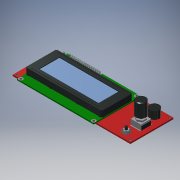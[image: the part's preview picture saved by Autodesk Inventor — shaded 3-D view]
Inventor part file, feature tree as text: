
AUTODESK INVENTOR PART (.ipt)
format: ipt  version: 2018 (Build 220112000, 112)  size: 651,776 bytes
history: native  units: mm
features: chamfer x1
ambient origin geometry x8: Origin, YZ Plane, XZ Plane, XY Plane, X Axis, Y Axis, Z Axis, Center Point
bodies: Solid1 (feature_tree)
feature tree (1):
  chamfer  "Chamfer6"  [1 undecoded]
note: 1 required parameter value undecoded (feature->parameter linkage not recoverable at this tier; creation-order binding heuristic only, values carry confidence <= 0.55)
